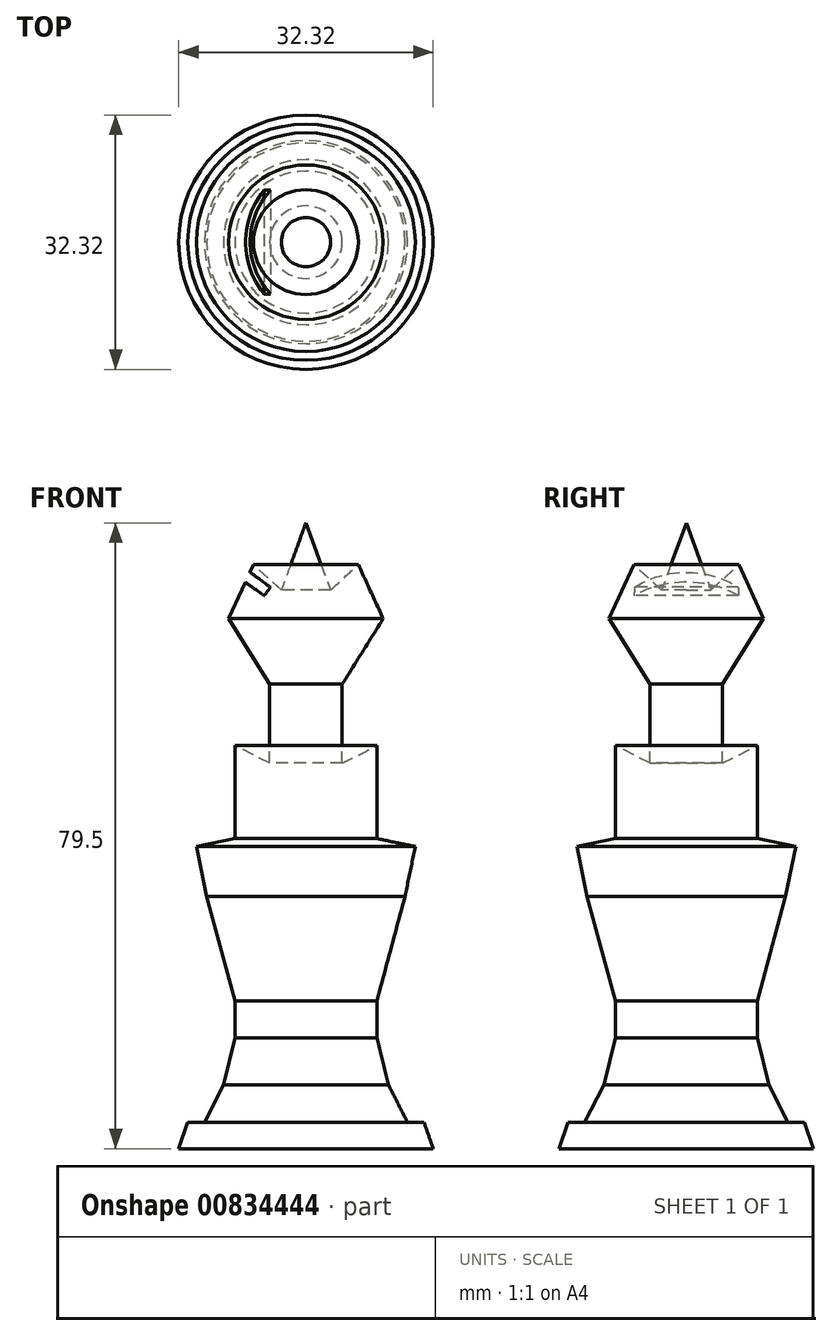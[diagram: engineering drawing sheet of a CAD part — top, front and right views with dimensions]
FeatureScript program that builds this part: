
annotation { "Feature Type Name" : "Feature", "Feature Type Description" : "" }
export const myFeature = defineFeature(function(context is Context, id is Id, definition is map)
    precondition{}
    {
        {
            var Q0;
            Q0=qCreatedBy(makeId("Front.planeOp"),FACE);
            var sketch = newSketch(context, id + "F0", { "sketchPlane" : qUnion([Q0])});
            skLineSegment(sketch, "E0", {"start": v(0, -22.56) * mm, "end": v(16.16, -22.56) * mm});
            skLineSegment(sketch, "E1", {"start": v(16.16, -22.56) * mm, "end": v(15, -19.2) * mm});
            skLineSegment(sketch, "E2", {"start": v(15, -19.2) * mm, "end": v(12.9, -19.2) * mm});
            skLineSegment(sketch, "E3", {"start": v(12.9, -19.2) * mm, "end": v(10.5, -14.48) * mm});
            skLineSegment(sketch, "E4", {"start": v(10.5, -14.48) * mm, "end": v(9.02, -8.49) * mm});
            skLineSegment(sketch, "E5", {"start": v(9.02, -8.49) * mm, "end": v(9.02, -3.76) * mm});
            skPoint(sketch, "E6.2.internal.orphan", {"position": v(0, 12.98) * mm});
            skPoint(sketch, "E6.3.internal.orphan", {"position": v(0, 13.24) * mm});
            skPoint(sketch, "E7.orphan", {"position": v(0, 32.77) * mm});
            skPoint(sketch, "E8.center.orphan", {"position": v(0, 27.98) * mm});
            skPoint(sketch, "E9.start.orphan", {"position": v(0, 25.3) * mm});
            skPoint(sketch, "E10.end.orphan", {"position": v(7.44, 23.14) * mm});
            skPoint(sketch, "E11.orphan", {"position": v(0, 35) * mm});
            skPoint(sketch, "E12.end.orphan", {"position": v(7.44, 30.15) * mm});
            skPoint(sketch, "E13.end.orphan", {"position": v(7.44, 3.9) * mm});
            skPoint(sketch, "E14.end.orphan", {"position": v(7.44, 0) * mm});
            skLineSegment(sketch, "E15", {"start": v(9.02, -3.76) * mm, "end": v(12.6, 9.51) * mm});
            skLineSegment(sketch, "E16", {"start": v(12.6, 9.51) * mm, "end": v(13.9, 15.83) * mm});
            skLineSegment(sketch, "E17", {"start": v(13.9, 15.83) * mm, "end": v(9.02, 16.83) * mm});
            skLineSegment(sketch, "E18", {"start": v(9.02, 16.83) * mm, "end": v(9.02, 28.64) * mm});
            skLineSegment(sketch, "E19", {"start": v(9.02, 28.64) * mm, "end": v(4.61, 26.41) * mm});
            skLineSegment(sketch, "E20", {"start": v(4.61, 26.41) * mm, "end": v(4.61, 36.44) * mm});
            skPoint(sketch, "E21.1.internal.orphan", {"position": v(4.61, 45.3) * mm});
            skPoint(sketch, "E21.2.internal.orphan", {"position": v(0, 47.67) * mm});
            skPoint(sketch, "E21.3.internal.orphan", {"position": v(0, 47.41) * mm});
            skLineSegment(sketch, "E22", {"start": v(0, 47.67) * mm, "end": v(0, 47.41) * mm});
            skPoint(sketch, "E23.orphan", {"position": v(0, 29.57) * mm});
            skLineSegment(sketch, "E24", {"start": v(0, 32.77) * mm, "end": v(0, -22.56) * mm});
            skPoint(sketch, "E25.orphan", {"position": v(0, 50.54) * mm});
            skPoint(sketch, "E26.orphan", {"position": v(0, 52.28) * mm});
            skPoint(sketch, "E27.orphan", {"position": v(0, 44.15) * mm});
            skPoint(sketch, "E28.start.orphan", {"position": v(4.61, 37.19) * mm});
            skLineSegment(sketch, "E29", {"start": v(4.61, 36.44) * mm, "end": v(9.81, 44.77) * mm});
            skLineSegment(sketch, "E30", {"start": v(9.81, 44.77) * mm, "end": v(6.66, 51.64) * mm});
            skLineSegment(sketch, "E31", {"start": v(6.66, 51.64) * mm, "end": v(3.13, 48.4) * mm});
            skLineSegment(sketch, "E32", {"start": v(3.13, 48.4) * mm, "end": v(0, 56.94) * mm});
            skLineSegment(sketch, "E33", {"start": v(0, 56.94) * mm, "end": v(0, 27.98) * mm});
            skSolve(sketch);
        }
        {
            var Q0;
            Q0 = qSketchRegion(id + "F0", true);
            var Q1;
            Q1=sQuery(id+"F0.wireOp",EDGE,"E33");
            revolve(context, id + "F1", {"surfaceOperationType" : NewSurfaceOperationType.NEW, "entities" : qUnion([Q0]), "axis" : qUnion([Q1]), "revolveType" : RevolveType.FULL});
        }
        {
            var Q0;
            Q0=qCreatedBy(makeId("Front.planeOp"),FACE);
            var sketch = newSketch(context, id + "F2", { "sketchPlane" : qUnion([Q0])});
            skLineSegment(sketch, "E34", {"start": v(-8.38, 51.58) * mm, "end": v(-4.5, 48.77) * mm});
            skLineSegment(sketch, "E35", {"start": v(-4.5, 48.77) * mm, "end": v(-5.3, 47.68) * mm});
            skLineSegment(sketch, "E36", {"start": v(-5.3, 47.68) * mm, "end": v(-9.14, 50.47) * mm});
            skLineSegment(sketch, "E37", {"start": v(-9.14, 50.47) * mm, "end": v(-8.38, 51.58) * mm});
            skSolve(sketch);
        }
        {
            var Q0;
            Q0 = qSketchRegion(id + "F2", true);
            extrude(context, id + "F3", {"entities" : qUnion([Q0]), "operationType" : NewBodyOperationType.REMOVE, "oppositeDirection" : true, "depth" : 25 * mm, "offsetDistance" : 25 * mm});
        }
        {
            var Q0;
            Q0 = qSketchRegion(id + "F2", true);
            extrude(context, id + "F4", {"entities" : qUnion([Q0]), "operationType" : NewBodyOperationType.REMOVE, "depth" : 25 * mm, "offsetDistance" : 25 * mm});
        }
    });
